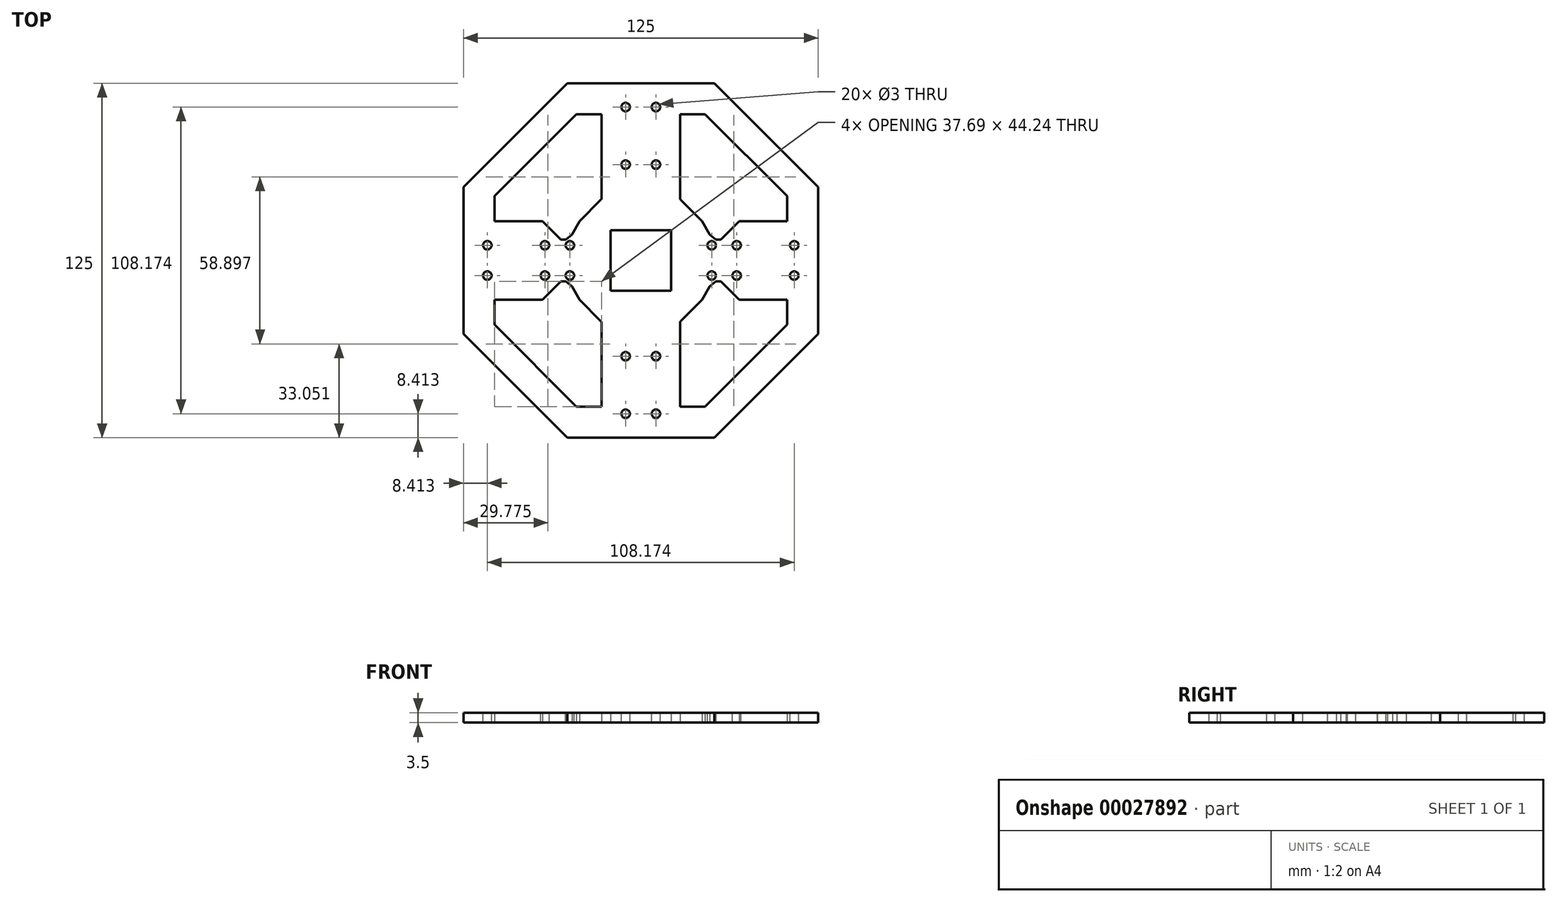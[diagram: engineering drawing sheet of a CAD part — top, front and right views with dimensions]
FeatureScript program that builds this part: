
annotation { "Feature Type Name" : "Feature", "Feature Type Description" : "" }
export const myFeature = defineFeature(function(context is Context, id is Id, definition is map)
    precondition{}
    {
        {
            var Q0;
            Q0=qCreatedBy(makeId("Top.planeOp"),FACE);
            var sketch = newSketch(context, id + "F0", { "sketchPlane" : qUnion([Q0])});
            skCircle(sketch, "E0.cCircle", {"center": v(0, 0) * mm, "radius": 62.5 * mm, "construction": true});
            skLineSegment(sketch, "E0.0", {"start": v(25.89, -62.5) * mm, "end": v(-25.89, -62.5) * mm});
            skLineSegment(sketch, "E0.1", {"start": v(-25.89, -62.5) * mm, "end": v(-62.5, -25.89) * mm});
            skLineSegment(sketch, "E0.2", {"start": v(-62.5, -25.89) * mm, "end": v(-62.5, 25.89) * mm});
            skLineSegment(sketch, "E0.3", {"start": v(-62.5, 25.89) * mm, "end": v(-25.89, 62.5) * mm});
            skLineSegment(sketch, "E0.4", {"start": v(-25.89, 62.5) * mm, "end": v(25.89, 62.5) * mm});
            skLineSegment(sketch, "E0.5", {"start": v(25.89, 62.5) * mm, "end": v(62.5, 25.89) * mm});
            skLineSegment(sketch, "E0.6", {"start": v(62.5, 25.89) * mm, "end": v(62.5, -25.89) * mm});
            skLineSegment(sketch, "E0.7", {"start": v(62.5, -25.89) * mm, "end": v(25.89, -62.5) * mm});
            skPoint(sketch, "E0.0.midPoint", {"position": v(0, -62.5) * mm});
            skLineSegment(sketch, "E1.rect.bottom", {"start": v(10.67, -10.67) * mm, "end": v(-10.67, -10.67) * mm});
            skLineSegment(sketch, "E1.rect.top", {"start": v(10.67, 10.67) * mm, "end": v(-10.67, 10.67) * mm});
            skLineSegment(sketch, "E1.rect.left", {"start": v(10.67, -10.67) * mm, "end": v(10.67, 10.67) * mm});
            skLineSegment(sketch, "E1.rect.right", {"start": v(-10.67, -10.67) * mm, "end": v(-10.67, 10.67) * mm});
            skLineSegment(sketch, "E2", {"start": v(-10.67, -10.67) * mm, "end": v(-62.5, -25.89) * mm, "construction": true});
            skLineSegment(sketch, "E3", {"start": v(-10.67, -10.67) * mm, "end": v(-25.89, -62.5) * mm, "construction": true});
            skLineSegment(sketch, "E4", {"start": v(-21.6, -13.88) * mm, "end": v(-13.88, -21.6) * mm});
            skLineSegment(sketch, "E5", {"start": v(-13.88, -21.6) * mm, "end": v(-22.68, -51.57) * mm});
            skLineSegment(sketch, "E6", {"start": v(-22.68, -51.57) * mm, "end": v(-51.57, -22.68) * mm});
            skLineSegment(sketch, "E7", {"start": v(-51.57, -22.68) * mm, "end": v(-21.6, -13.88) * mm});
            skLineSegment(sketch, "E8.1.1", {"start": v(51.57, -22.68) * mm, "end": v(22.68, -51.57) * mm});
            skLineSegment(sketch, "E8.1.2", {"start": v(21.6, -13.88) * mm, "end": v(51.57, -22.68) * mm});
            skLineSegment(sketch, "E8.1.3", {"start": v(22.68, -51.57) * mm, "end": v(13.88, -21.6) * mm});
            skLineSegment(sketch, "E8.1.4", {"start": v(13.88, -21.6) * mm, "end": v(21.6, -13.88) * mm});
            skLineSegment(sketch, "E8.2.1", {"start": v(22.68, 51.57) * mm, "end": v(51.57, 22.68) * mm});
            skLineSegment(sketch, "E8.2.2", {"start": v(13.88, 21.6) * mm, "end": v(22.68, 51.57) * mm});
            skLineSegment(sketch, "E8.2.3", {"start": v(51.57, 22.68) * mm, "end": v(21.6, 13.88) * mm});
            skLineSegment(sketch, "E8.2.4", {"start": v(21.6, 13.88) * mm, "end": v(13.88, 21.6) * mm});
            skLineSegment(sketch, "E8.3.1", {"start": v(-51.57, 22.68) * mm, "end": v(-22.68, 51.57) * mm});
            skLineSegment(sketch, "E8.3.2", {"start": v(-21.6, 13.88) * mm, "end": v(-51.57, 22.68) * mm});
            skLineSegment(sketch, "E8.3.3", {"start": v(-22.68, 51.57) * mm, "end": v(-13.88, 21.6) * mm});
            skLineSegment(sketch, "E8.3.4", {"start": v(-13.88, 21.6) * mm, "end": v(-21.6, 13.88) * mm});
            skLineSegment(sketch, "E9", {"start": v(-21.6, -13.88) * mm, "end": v(-51.57, -13.88) * mm});
            skLineSegment(sketch, "E10", {"start": v(-51.57, -13.88) * mm, "end": v(-51.57, -22.68) * mm});
            skLineSegment(sketch, "E11", {"start": v(-22.68, -51.57) * mm, "end": v(-13.88, -51.57) * mm});
            skLineSegment(sketch, "E12", {"start": v(-13.88, -51.57) * mm, "end": v(-13.88, -21.6) * mm});
            skLineSegment(sketch, "E13.1.1", {"start": v(51.57, -22.68) * mm, "end": v(51.57, -13.88) * mm});
            skLineSegment(sketch, "E13.1.2", {"start": v(51.57, -13.88) * mm, "end": v(21.6, -13.88) * mm});
            skLineSegment(sketch, "E13.1.3", {"start": v(13.88, -21.6) * mm, "end": v(13.88, -51.57) * mm});
            skLineSegment(sketch, "E13.1.4", {"start": v(13.88, -51.57) * mm, "end": v(22.68, -51.57) * mm});
            skLineSegment(sketch, "E13.2.1", {"start": v(22.68, 51.57) * mm, "end": v(13.88, 51.57) * mm});
            skLineSegment(sketch, "E13.2.2", {"start": v(13.88, 51.57) * mm, "end": v(13.88, 21.6) * mm});
            skLineSegment(sketch, "E13.2.3", {"start": v(21.6, 13.88) * mm, "end": v(51.57, 13.88) * mm});
            skLineSegment(sketch, "E13.2.4", {"start": v(51.57, 13.88) * mm, "end": v(51.57, 22.68) * mm});
            skLineSegment(sketch, "E13.3.1", {"start": v(-51.57, 22.68) * mm, "end": v(-51.57, 13.88) * mm});
            skLineSegment(sketch, "E13.3.2", {"start": v(-51.57, 13.88) * mm, "end": v(-21.6, 13.88) * mm});
            skLineSegment(sketch, "E13.3.3", {"start": v(-13.88, 21.6) * mm, "end": v(-13.88, 51.57) * mm});
            skLineSegment(sketch, "E13.3.4", {"start": v(-13.88, 51.57) * mm, "end": v(-22.68, 51.57) * mm});
            skLineSegment(sketch, "E14", {"start": v(21.6, 13.88) * mm, "end": v(28.16, 7.33) * mm});
            skLineSegment(sketch, "E15", {"start": v(28.16, 7.33) * mm, "end": v(34.7, 13.88) * mm});
            skLineSegment(sketch, "E16.MirrorCS", {"start": v(-21.6, 13.88) * mm, "end": v(-28.16, 7.33) * mm});
            skLineSegment(sketch, "E17.MirrorCS", {"start": v(-28.16, 7.33) * mm, "end": v(-34.7, 13.88) * mm});
            skLineSegment(sketch, "E18.MirrorCS", {"start": v(-28.16, -7.33) * mm, "end": v(-34.7, -13.88) * mm});
            skLineSegment(sketch, "E19.MirrorCS", {"start": v(-21.6, -13.88) * mm, "end": v(-28.16, -7.33) * mm});
            skLineSegment(sketch, "E20.MirrorCS", {"start": v(21.6, -13.88) * mm, "end": v(28.16, -7.33) * mm});
            skLineSegment(sketch, "E21.MirrorCS", {"start": v(28.16, -7.33) * mm, "end": v(34.7, -13.88) * mm});
            skLineSegment(sketch, "E22.MirrorCS", {"start": v(6.74, 28.75) * mm, "end": v(13.88, 35.89) * mm});
            skLineSegment(sketch, "E23.MirrorCS", {"start": v(13.88, 21.6) * mm, "end": v(6.74, 28.75) * mm});
            skLineSegment(sketch, "E24", {"start": v(-37.12, 37.12) * mm, "end": v(37.12, -37.12) * mm, "construction": true});
            skLineSegment(sketch, "E25", {"start": v(37.12, 37.12) * mm, "end": v(-37.12, -37.12) * mm, "construction": true});
            skLineSegment(sketch, "E26.MirrorCS", {"start": v(-7.33, -28.16) * mm, "end": v(-13.88, -34.7) * mm});
            skLineSegment(sketch, "E27.MirrorCS", {"start": v(-13.88, -21.6) * mm, "end": v(-7.33, -28.16) * mm});
            skLineSegment(sketch, "E28.MirrorCS", {"start": v(13.88, -21.6) * mm, "end": v(7.33, -28.16) * mm});
            skLineSegment(sketch, "E29.MirrorCS", {"start": v(7.33, -28.16) * mm, "end": v(13.88, -34.7) * mm});
            skLineSegment(sketch, "E30.MirrorCS", {"start": v(-7.33, 28.16) * mm, "end": v(-13.88, 34.7) * mm});
            skLineSegment(sketch, "E31.MirrorCS", {"start": v(-13.88, 21.6) * mm, "end": v(-7.33, 28.16) * mm});
            skLineSegment(sketch, "E32", {"start": v(-28.16, 7.33) * mm, "end": v(-25.23, 7.33) * mm});
            skLineSegment(sketch, "E33", {"start": v(-25.23, 7.33) * mm, "end": v(-21.6, 13.88) * mm});
            skLineSegment(sketch, "E34.MirrorCS", {"start": v(-28.16, -7.33) * mm, "end": v(-25.23, -7.33) * mm});
            skLineSegment(sketch, "E35.MirrorCS", {"start": v(-25.23, -7.33) * mm, "end": v(-21.6, -13.88) * mm});
            skLineSegment(sketch, "E36.MirrorCS", {"start": v(28.16, 7.33) * mm, "end": v(25.23, 7.33) * mm});
            skLineSegment(sketch, "E37.MirrorCS", {"start": v(25.23, 7.33) * mm, "end": v(21.6, 13.88) * mm});
            skLineSegment(sketch, "E38.MirrorCS", {"start": v(28.16, -7.33) * mm, "end": v(25.23, -7.33) * mm});
            skLineSegment(sketch, "E39.MirrorCS", {"start": v(25.23, -7.33) * mm, "end": v(21.6, -13.88) * mm});
            skLineSegment(sketch, "E40", {"start": v(-26.44, 7.33) * mm, "end": v(-24.23, 9.15) * mm});
            skLineSegment(sketch, "E41.MirrorCS", {"start": v(-26.44, -7.33) * mm, "end": v(-24.23, -9.15) * mm});
            skLineSegment(sketch, "E42.MirrorCS", {"start": v(26.44, 7.33) * mm, "end": v(24.23, 9.15) * mm});
            skLineSegment(sketch, "E43.MirrorCS", {"start": v(26.44, -7.33) * mm, "end": v(24.23, -9.15) * mm});
            skSolve(sketch);
        }
        {
            var Q0;
            Q0 = qSketchRegion(id + "F0", true);
            var Q1;
            {var subQ0=sQuery(id+"F0.wireOp",EDGE,"E40");Q1=makeQuery(id+"F0.imprint","IMPRINT",FACE,{"disambiguationData":[TD([[makeQuery(id+"F0.imprint","IMPRINT",EDGE,{"derivedFrom":subQ0}),-1.0]])]});}
            var Q2;
            {var subQ0=sQuery(id+"F0.wireOp",EDGE,"E41.MirrorCS");Q2=makeQuery(id+"F0.imprint","IMPRINT",FACE,{"disambiguationData":[TD([[makeQuery(id+"F0.imprint","IMPRINT",EDGE,{"derivedFrom":subQ0}),1.0]])]});}
            var Q3;
            {var subQ0=sQuery(id+"F0.wireOp",EDGE,"E42.MirrorCS");Q3=makeQuery(id+"F0.imprint","IMPRINT",FACE,{"disambiguationData":[TD([[makeQuery(id+"F0.imprint","IMPRINT",EDGE,{"derivedFrom":subQ0}),1.0]])]});}
            var Q4;
            {var subQ0=sQuery(id+"F0.wireOp",EDGE,"E43.MirrorCS");Q4=makeQuery(id+"F0.imprint","IMPRINT",FACE,{"disambiguationData":[TD([[makeQuery(id+"F0.imprint","IMPRINT",EDGE,{"derivedFrom":subQ0}),-1.0]])]});}
            var Q5;
            {var subQ1=sQuery(id+"F0.wireOp",EDGE,"E30.MirrorCS");Q5=makeQuery(id+"F0.imprint","IMPRINT",FACE,{"disambiguationData":[TD([[makeQuery(id+"F0.imprint","IMPRINT",EDGE,{"derivedFrom":subQ1}),1.0]])]});}
            var Q6;
            {var subQ1=sQuery(id+"F0.wireOp",EDGE,"E22.MirrorCS");Q6=makeQuery(id+"F0.imprint","IMPRINT",FACE,{"disambiguationData":[TD([[makeQuery(id+"F0.imprint","IMPRINT",EDGE,{"derivedFrom":subQ1}),-1.0]])]});}
            var Q7;
            {var subQ1=sQuery(id+"F0.wireOp",EDGE,"E26.MirrorCS");Q7=makeQuery(id+"F0.imprint","IMPRINT",FACE,{"disambiguationData":[TD([[makeQuery(id+"F0.imprint","IMPRINT",EDGE,{"derivedFrom":subQ1}),-1.0]])]});}
            var Q8;
            {var subQ1=sQuery(id+"F0.wireOp",EDGE,"E28.MirrorCS");Q8=makeQuery(id+"F0.imprint","IMPRINT",FACE,{"disambiguationData":[TD([[makeQuery(id+"F0.imprint","IMPRINT",EDGE,{"derivedFrom":subQ1}),1.0]])]});}
            extrude(context, id + "F1", {"entities" : qUnion([Q0, Q1, Q2, Q3, Q4, Q5, Q6, Q7, Q8]), "depth" : 3.5 * mm});
        }
        {
            var Q0;
            Q0=makeQuery(id+"F1.opExtrude","CAP_FACE",FACE,{"disambiguationData":[OSD([sQuery(id+"F0.wireOp",EDGE,"E0.0"),sQuery(id+"F0.wireOp",EDGE,"E0.1"),sQuery(id+"F0.wireOp",EDGE,"E0.2"),sQuery(id+"F0.wireOp",EDGE,"E0.3"),sQuery(id+"F0.wireOp",EDGE,"E0.4"),sQuery(id+"F0.wireOp",EDGE,"E0.5"),sQuery(id+"F0.wireOp",EDGE,"E0.6"),sQuery(id+"F0.wireOp",EDGE,"E0.7"),sQuery(id+"F0.wireOp",EDGE,"E1.rect.bottom"),sQuery(id+"F0.wireOp",EDGE,"E1.rect.top"),sQuery(id+"F0.wireOp",EDGE,"E1.rect.left"),sQuery(id+"F0.wireOp",EDGE,"E1.rect.right"),sQuery(id+"F0.wireOp",EDGE,"E4"),sQuery(id+"F0.wireOp",EDGE,"E6"),sQuery(id+"F0.wireOp",EDGE,"E8.1.1"),sQuery(id+"F0.wireOp",EDGE,"E8.1.4"),sQuery(id+"F0.wireOp",EDGE,"E8.2.1"),sQuery(id+"F0.wireOp",EDGE,"E8.2.4"),sQuery(id+"F0.wireOp",EDGE,"E8.3.1"),sQuery(id+"F0.wireOp",EDGE,"E8.3.4"),sQuery(id+"F0.wireOp",EDGE,"E9"),sQuery(id+"F0.wireOp",EDGE,"E10"),sQuery(id+"F0.wireOp",EDGE,"E11"),sQuery(id+"F0.wireOp",EDGE,"E12"),sQuery(id+"F0.wireOp",EDGE,"E13.1.1"),sQuery(id+"F0.wireOp",EDGE,"E13.1.2"),sQuery(id+"F0.wireOp",EDGE,"E13.1.3"),sQuery(id+"F0.wireOp",EDGE,"E13.1.4"),sQuery(id+"F0.wireOp",EDGE,"E13.2.1"),sQuery(id+"F0.wireOp",EDGE,"E13.2.2"),sQuery(id+"F0.wireOp",EDGE,"E13.2.3"),sQuery(id+"F0.wireOp",EDGE,"E13.2.4"),sQuery(id+"F0.wireOp",EDGE,"E13.3.1"),sQuery(id+"F0.wireOp",EDGE,"E13.3.2"),sQuery(id+"F0.wireOp",EDGE,"E13.3.3"),sQuery(id+"F0.wireOp",EDGE,"E13.3.4")])],"isStart":false});
            var sketch = newSketch(context, id + "F2", { "sketchPlane" : qUnion([Q0])});
            skCircle(sketch, "E44", {"center": v(-33.79, 5.34) * mm, "radius": 1.5 * mm});
            skCircle(sketch, "E45.MirrorC", {"center": v(-33.79, -5.34) * mm, "radius": 1.5 * mm});
            skLineSegment(sketch, "E46", {"start": v(-43.94, -7.27) * mm, "end": v(-43.94, 7.73) * mm, "construction": true});
            skCircle(sketch, "E47.MirrorC", {"center": v(-54.09, 5.34) * mm, "radius": 1.5 * mm});
            skCircle(sketch, "E48.MirrorC", {"center": v(-54.09, -5.34) * mm, "radius": 1.5 * mm});
            skLineSegment(sketch, "E49", {"start": v(-54.16, -6.84) * mm, "end": v(-33.79, -6.84) * mm, "construction": true});
            skCircle(sketch, "E50.1.0", {"center": v(-5.34, -33.79) * mm, "radius": 1.5 * mm});
            skCircle(sketch, "E50.1.1", {"center": v(5.34, -33.79) * mm, "radius": 1.5 * mm});
            skCircle(sketch, "E50.1.2", {"center": v(-5.34, -54.09) * mm, "radius": 1.5 * mm});
            skCircle(sketch, "E50.1.3", {"center": v(5.34, -54.09) * mm, "radius": 1.5 * mm});
            skCircle(sketch, "E50.2.0", {"center": v(33.79, -5.34) * mm, "radius": 1.5 * mm});
            skCircle(sketch, "E50.2.1", {"center": v(33.79, 5.34) * mm, "radius": 1.5 * mm});
            skCircle(sketch, "E50.2.2", {"center": v(54.09, -5.34) * mm, "radius": 1.5 * mm});
            skCircle(sketch, "E50.2.3", {"center": v(54.09, 5.34) * mm, "radius": 1.5 * mm});
            skCircle(sketch, "E50.3.0", {"center": v(5.34, 33.79) * mm, "radius": 1.5 * mm});
            skCircle(sketch, "E50.3.1", {"center": v(-5.34, 33.79) * mm, "radius": 1.5 * mm});
            skCircle(sketch, "E50.3.2", {"center": v(5.34, 54.09) * mm, "radius": 1.5 * mm});
            skCircle(sketch, "E50.3.3", {"center": v(-5.34, 54.09) * mm, "radius": 1.5 * mm});
            skPoint(sketch, "E50.center", {"position": v(0, 0) * mm});
            skCircle(sketch, "E51", {"center": v(-25, 5.33) * mm, "radius": 1.5 * mm});
            skCircle(sketch, "E52.MirrorC", {"center": v(25, 5.33) * mm, "radius": 1.5 * mm});
            skCircle(sketch, "E53.MirrorC", {"center": v(25, -5.33) * mm, "radius": 1.5 * mm});
            skCircle(sketch, "E54.MirrorC", {"center": v(-25, -5.33) * mm, "radius": 1.5 * mm});
            skSolve(sketch);
        }
        {
            var Q0;
            Q0 = qSketchRegion(id + "F2", true);
            extrude(context, id + "F3", {"entities" : qUnion([Q0]), "operationType" : NewBodyOperationType.REMOVE, "oppositeDirection" : true, "depth" : 25 * mm});
        }
        {
            var Q0;
            Q0=makeQuery(id+"F1.opExtrude","SWEPT_EDGE",EDGE,{"disambiguationData":[OSD([sQuery(id+"F0.wireOp",EDGE,"E16.MirrorCS"),sQuery(id+"F0.wireOp",EDGE,"E17.MirrorCS")])]});
            var Q1;
            Q1=makeQuery(id+"F1.opExtrude","SWEPT_EDGE",EDGE,{"disambiguationData":[OSD([sQuery(id+"F0.wireOp",EDGE,"E18.MirrorCS"),sQuery(id+"F0.wireOp",EDGE,"E19.MirrorCS")])]});
            var Q2;
            Q2=makeQuery(id+"F1.opExtrude","SWEPT_EDGE",EDGE,{"disambiguationData":[OSD([sQuery(id+"F0.wireOp",EDGE,"E20.MirrorCS"),sQuery(id+"F0.wireOp",EDGE,"E21.MirrorCS")])]});
            var Q3;
            Q3=makeQuery(id+"F1.opExtrude","SWEPT_EDGE",EDGE,{"disambiguationData":[OSD([sQuery(id+"F0.wireOp",EDGE,"E28.MirrorCS"),sQuery(id+"F0.wireOp",EDGE,"E29.MirrorCS")])]});
            var Q4;
            Q4=makeQuery(id+"F1.opExtrude","SWEPT_EDGE",EDGE,{"disambiguationData":[OSD([sQuery(id+"F0.wireOp",EDGE,"E22.MirrorCS"),sQuery(id+"F0.wireOp",EDGE,"E23.MirrorCS")])]});
            var Q5;
            Q5=makeQuery(id+"F1.opExtrude","SWEPT_EDGE",EDGE,{"disambiguationData":[OSD([sQuery(id+"F0.wireOp",EDGE,"E14"),sQuery(id+"F0.wireOp",EDGE,"E15")])]});
            var Q6;
            Q6=makeQuery(id+"F1.opExtrude","SWEPT_EDGE",EDGE,{"disambiguationData":[OSD([sQuery(id+"F0.wireOp",EDGE,"E30.MirrorCS"),sQuery(id+"F0.wireOp",EDGE,"E31.MirrorCS")])]});
            var Q7;
            Q7=makeQuery(id+"F1.opExtrude","SWEPT_EDGE",EDGE,{"disambiguationData":[OSD([sQuery(id+"F0.wireOp",EDGE,"E26.MirrorCS"),sQuery(id+"F0.wireOp",EDGE,"E27.MirrorCS")])]});
            fillet(context, id + "F4", {"entities" : qUnion([Q0, Q1, Q2, Q3, Q4, Q5, Q6, Q7]), "radius" : 0.5 * mm, "tangentPropagation" : true, "allowEdgeOverflow" : false});
        }
    });
